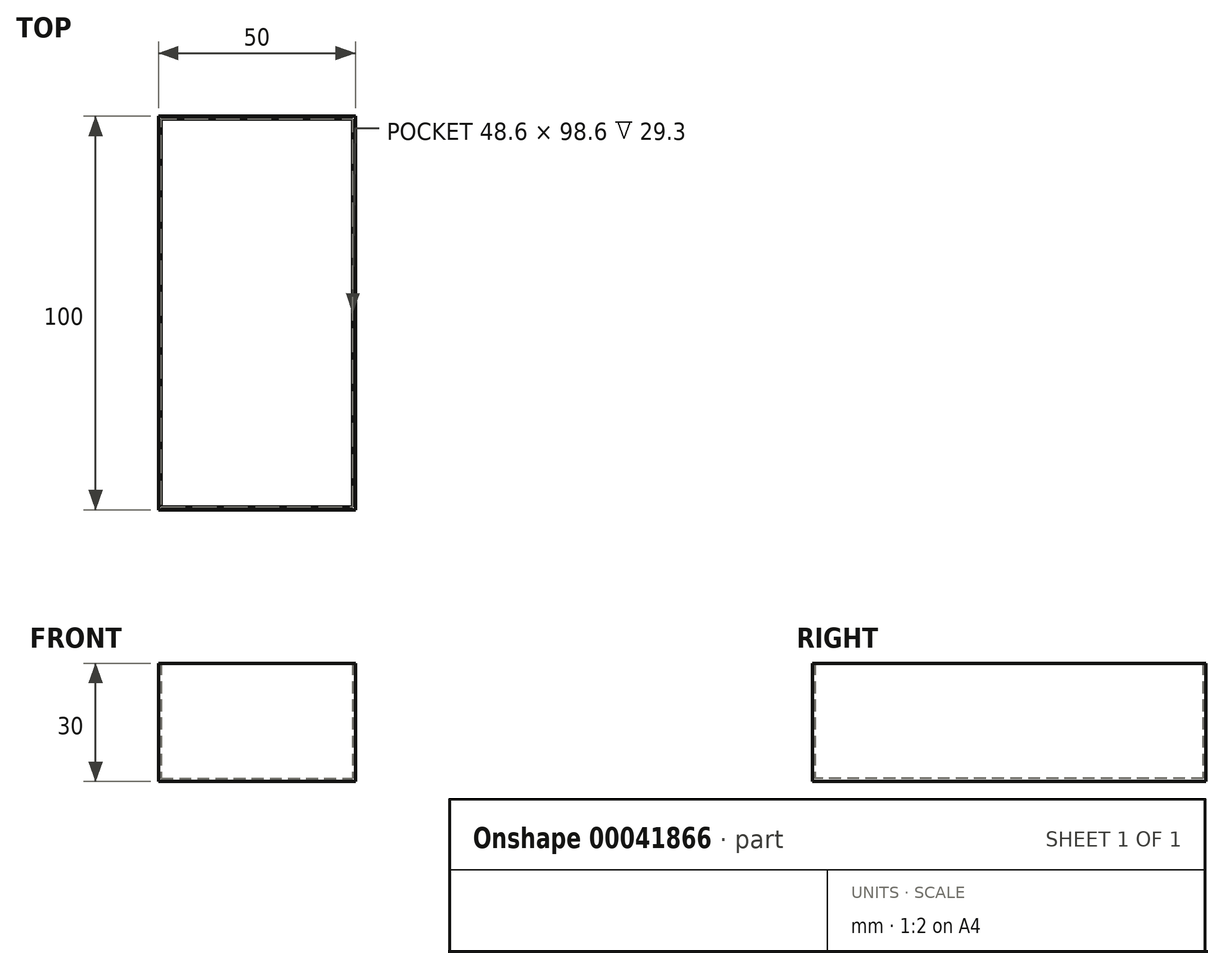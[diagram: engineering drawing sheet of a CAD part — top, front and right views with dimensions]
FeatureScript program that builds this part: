
annotation { "Feature Type Name" : "Feature", "Feature Type Description" : "" }
export const myFeature = defineFeature(function(context is Context, id is Id, definition is map)
    precondition{}
    {
        {
            var Q0;
            Q0=qCreatedBy(makeId("Top.planeOp"),FACE);
            var sketch = newSketch(context, id + "F0", { "sketchPlane" : qUnion([Q0])});
            skLineSegment(sketch, "E0.bottom", {"start": v(-49.13, 49.46) * mm, "end": v(0.87, 49.46) * mm});
            skLineSegment(sketch, "E0.top", {"start": v(-49.13, -50.54) * mm, "end": v(0.87, -50.54) * mm});
            skLineSegment(sketch, "E0.left", {"start": v(-49.13, 49.46) * mm, "end": v(-49.13, -50.54) * mm});
            skLineSegment(sketch, "E0.right", {"start": v(0.87, 49.46) * mm, "end": v(0.87, -50.54) * mm});
            skSolve(sketch);
        }
        {
            var Q0;
            Q0=qSketchRegion(id+"F0",true);
            extrude(context, id + "F1", {"entities" : qUnion([Q0]), "depth" : 30 * mm});
        }
        {
            var Q0;
            Q0=makeQuery(id+"F1.opExtrude","CAP_FACE",FACE,{"disambiguationData":[OSD([sQuery(id+"F0.wireOp",EDGE,"E0.bottom"),sQuery(id+"F0.wireOp",EDGE,"E0.top"),sQuery(id+"F0.wireOp",EDGE,"E0.left"),sQuery(id+"F0.wireOp",EDGE,"E0.right")])],"isStart":false});
            shell(context, id + "F2", {"entities" : qUnion([Q0]), "thickness" : 0.7 * mm});
        }
    });
